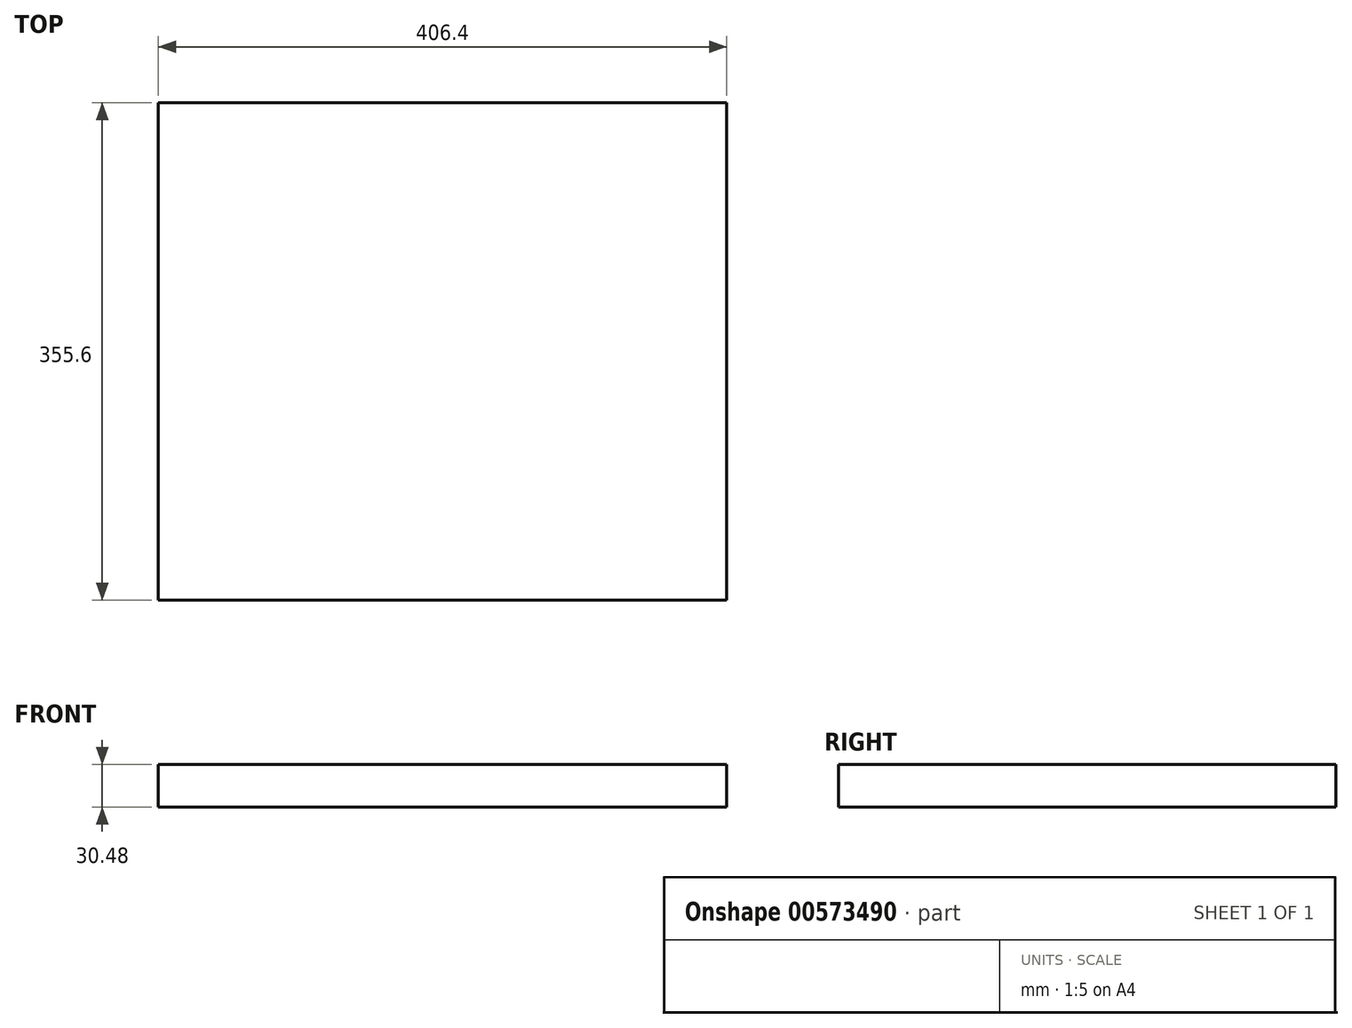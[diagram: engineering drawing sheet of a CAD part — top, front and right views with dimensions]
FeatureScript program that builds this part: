
annotation { "Feature Type Name" : "Feature", "Feature Type Description" : "" }
export const myFeature = defineFeature(function(context is Context, id is Id, definition is map)
    precondition{}
    {
        {
            var Q0;
            Q0=qCreatedBy(makeId("Top.planeOp"),FACE);
            var sketch = newSketch(context, id + "F0", { "sketchPlane" : qUnion([Q0])});
            skLineSegment(sketch, "E0.bottom", {"start": v(20.88, 0) * mm, "end": v(427.28, 0) * mm});
            skLineSegment(sketch, "E0.top", {"start": v(20.88, 355.6) * mm, "end": v(427.28, 355.6) * mm});
            skLineSegment(sketch, "E0.left", {"start": v(20.88, 0) * mm, "end": v(20.88, 355.6) * mm});
            skLineSegment(sketch, "E0.right", {"start": v(427.28, 0) * mm, "end": v(427.28, 355.6) * mm});
            skSolve(sketch);
        }
        {
            var Q0;
            Q0=makeQuery(id+"F0.imprint","IMPRINT",FACE,{"disambiguationData":[TD([[makeQuery(id+"F0.imprint","IMPRINT",EDGE,{"derivedFrom":sQuery(id+"F0.wireOp",EDGE,"E0.bottom")}),1.0]])]});
            extrude(context, id + "F1", {"entities" : qUnion([Q0]), "depth" : 30.48 * mm, "offsetDistance" : 25.4 * mm});
        }
    });
